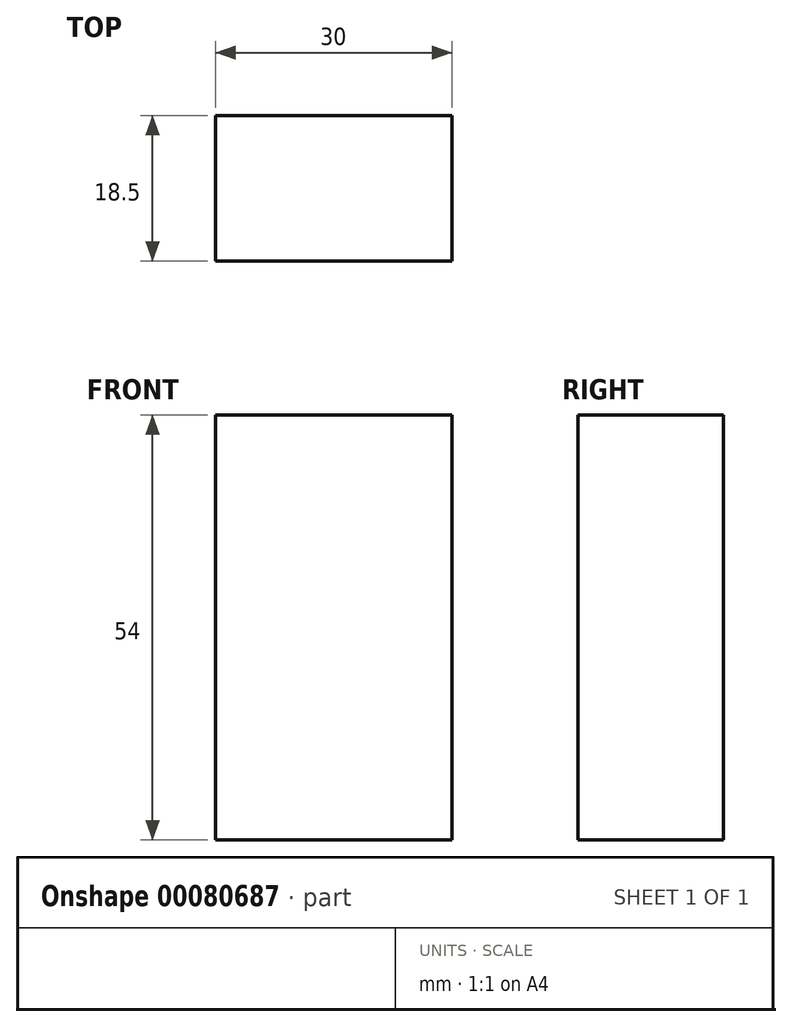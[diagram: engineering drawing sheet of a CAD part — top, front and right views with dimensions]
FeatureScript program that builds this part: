
annotation { "Feature Type Name" : "Feature", "Feature Type Description" : "" }
export const myFeature = defineFeature(function(context is Context, id is Id, definition is map)
    precondition{}
    {
        {
            var Q0;
            Q0=qCreatedBy(makeId("Front.planeOp"),FACE);
            var sketch = newSketch(context, id + "F0", { "sketchPlane" : qUnion([Q0])});
            skLineSegment(sketch, "E0.bottom", {"start": v(-15, 27) * mm, "end": v(15, 27) * mm});
            skLineSegment(sketch, "E0.top", {"start": v(-15, -27) * mm, "end": v(15, -27) * mm});
            skLineSegment(sketch, "E0.left", {"start": v(-15, 27) * mm, "end": v(-15, -27) * mm});
            skLineSegment(sketch, "E0.right", {"start": v(15, 27) * mm, "end": v(15, -27) * mm});
            skPoint(sketch, "E0.middle", {"position": v(0, 0) * mm});
            skSolve(sketch);
        }
        {
            var Q0;
            Q0=makeQuery(id+"F0.imprint","IMPRINT",FACE,{"disambiguationData":[TD([[makeQuery(id+"F0.imprint","IMPRINT",EDGE,{"derivedFrom":sQuery(id+"F0.wireOp",EDGE,"E0.bottom")}),-1.0]])]});
            extrude(context, id + "F1", {"entities" : qUnion([Q0]), "depth" : 18.5 * mm});
        }
    });
